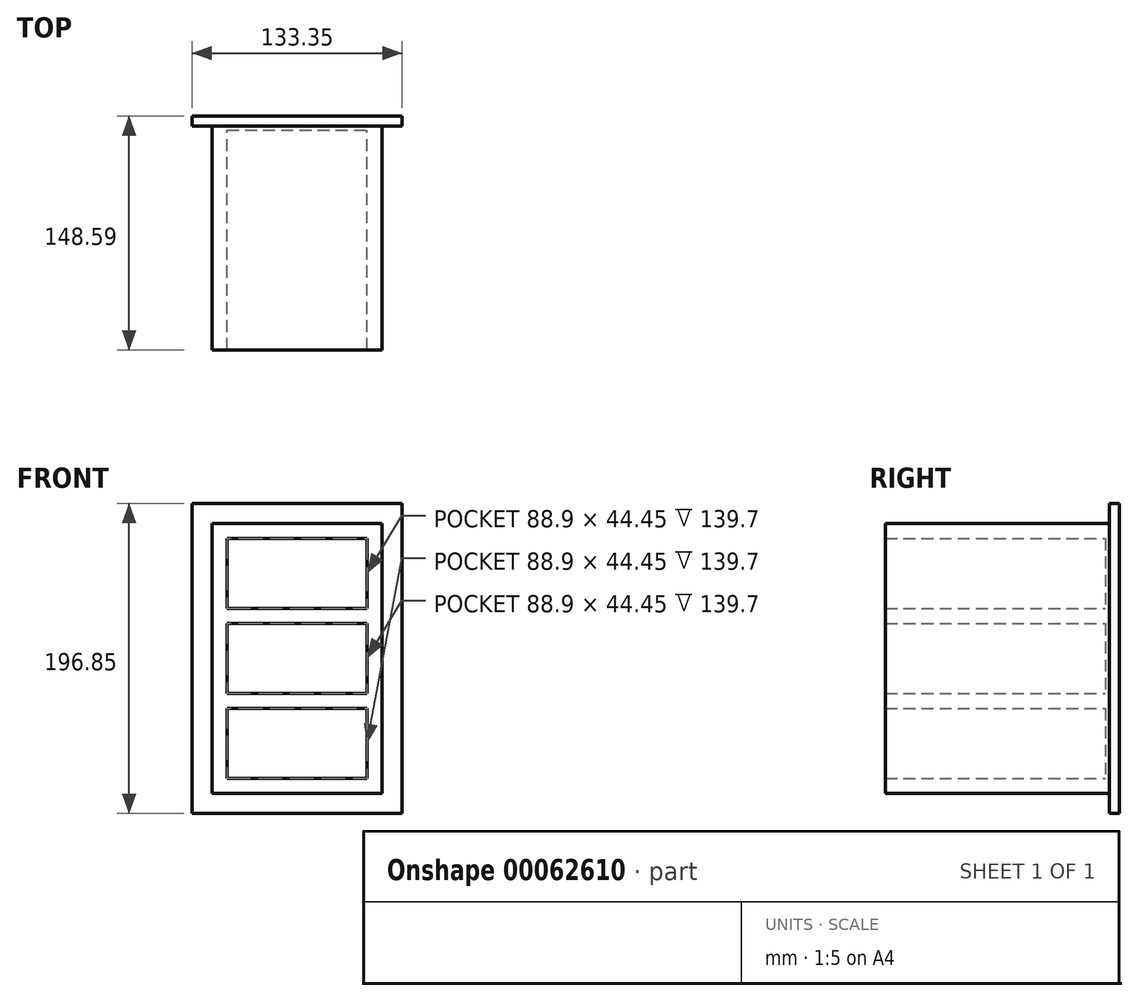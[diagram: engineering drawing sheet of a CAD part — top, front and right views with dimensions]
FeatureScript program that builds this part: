
annotation { "Feature Type Name" : "Feature", "Feature Type Description" : "" }
export const myFeature = defineFeature(function(context is Context, id is Id, definition is map)
    precondition{}
    {
        {
            var Q0;
            Q0=qCreatedBy(makeId("Front.planeOp"),FACE);
            var sketch = newSketch(context, id + "F0", { "sketchPlane" : qUnion([Q0])});
            skLineSegment(sketch, "E0.bottom", {"start": v(-98.78, 89.68) * mm, "end": v(-9.88, 89.68) * mm});
            skLineSegment(sketch, "E0.top", {"start": v(-98.78, -62.72) * mm, "end": v(-9.88, -62.72) * mm});
            skLineSegment(sketch, "E0.left", {"start": v(-98.78, 89.68) * mm, "end": v(-98.78, 45.23) * mm});
            skLineSegment(sketch, "E0.right", {"start": v(-9.88, 89.68) * mm, "end": v(-9.88, 45.23) * mm});
            skLineSegment(sketch, "E1.bottom", {"start": v(-98.78, 45.23) * mm, "end": v(-9.88, 45.23) * mm});
            skLineSegment(sketch, "E1.top", {"start": v(-98.78, 35.7) * mm, "end": v(-9.88, 35.7) * mm});
            skLineSegment(sketch, "E2", {"start": v(-98.78, 35.7) * mm, "end": v(-98.78, -8.75) * mm});
            skLineSegment(sketch, "E3.bottom", {"start": v(-98.78, -8.75) * mm, "end": v(-9.88, -8.75) * mm});
            skLineSegment(sketch, "E3.top", {"start": v(-98.78, -18.27) * mm, "end": v(-9.88, -18.27) * mm});
            skLineSegment(sketch, "E4", {"start": v(-98.78, -18.27) * mm, "end": v(-98.78, -62.72) * mm});
            skLineSegment(sketch, "E5.bottom", {"start": v(-108.3, 99.2) * mm, "end": v(-0.36, 99.2) * mm});
            skLineSegment(sketch, "E5.top", {"start": v(-108.3, -72.25) * mm, "end": v(-0.36, -72.25) * mm});
            skLineSegment(sketch, "E5.left", {"start": v(-108.3, 99.2) * mm, "end": v(-108.3, -72.25) * mm});
            skLineSegment(sketch, "E5.right", {"start": v(-0.36, 99.2) * mm, "end": v(-0.36, -72.25) * mm});
            skPoint(sketch, "E6.end.orphan", {"position": v(-108.3, 13.48) * mm});
            skPoint(sketch, "E6.start.orphan", {"position": v(-98.78, 13.48) * mm});
            skPoint(sketch, "E7.start.orphan", {"position": v(-54.33, 89.68) * mm});
            skPoint(sketch, "E8.end.orphan", {"position": v(-0.36, 13.48) * mm});
            skPoint(sketch, "E8.start.orphan", {"position": v(-9.88, 13.48) * mm});
            skPoint(sketch, "E9.start.orphan", {"position": v(-54.33, -62.72) * mm});
            skLineSegment(sketch, "E10.trimOffspring", {"start": v(-9.88, -18.27) * mm, "end": v(-9.88, -62.72) * mm});
            skLineSegment(sketch, "E11.trimOffspring", {"start": v(-9.88, 35.7) * mm, "end": v(-9.88, -8.75) * mm});
            skSolve(sketch);
        }
        {
            var Q0;
            Q0=makeQuery(id+"F0.imprint","IMPRINT",FACE,{"disambiguationData":[TD([[makeQuery(id+"F0.imprint","IMPRINT",EDGE,{"derivedFrom":sQuery(id+"F0.wireOp",EDGE,"E0.bottom")}),1.0]])]});
            extrude(context, id + "F1", {"entities" : qUnion([Q0]), "depth" : 139.7 * mm});
        }
        {
            var Q0;
            Q0=makeQuery(id+"F1.opExtrude","CAP_FACE",FACE,{"disambiguationData":[OSD([sQuery(id+"F0.wireOp",EDGE,"E0.bottom"),sQuery(id+"F0.wireOp",EDGE,"E0.top"),sQuery(id+"F0.wireOp",EDGE,"E0.right"),sQuery(id+"F0.wireOp",EDGE,"E0.left"),sQuery(id+"F0.wireOp",EDGE,"E1.bottom"),sQuery(id+"F0.wireOp",EDGE,"E1.top"),sQuery(id+"F0.wireOp",EDGE,"E3.bottom"),sQuery(id+"F0.wireOp",EDGE,"E3.top"),sQuery(id+"F0.wireOp",EDGE,"E5.bottom"),sQuery(id+"F0.wireOp",EDGE,"E5.top"),sQuery(id+"F0.wireOp",EDGE,"E5.left"),sQuery(id+"F0.wireOp",EDGE,"E5.right"),sQuery(id+"F0.wireOp",EDGE,"E2"),sQuery(id+"F0.wireOp",EDGE,"E4"),sQuery(id+"F0.wireOp",EDGE,"E10.trimOffspring"),sQuery(id+"F0.wireOp",EDGE,"E11.trimOffspring")])],"isStart":true});
            var sketch = newSketch(context, id + "F2", { "sketchPlane" : qUnion([Q0])});
            skLineSegment(sketch, "E12.bottom", {"start": v(0.36, 99.2) * mm, "end": v(108.3, 99.2) * mm});
            skLineSegment(sketch, "E12.top", {"start": v(0.36, -72.25) * mm, "end": v(108.3, -72.25) * mm});
            skLineSegment(sketch, "E12.left", {"start": v(0.36, 99.2) * mm, "end": v(0.36, -72.25) * mm});
            skLineSegment(sketch, "E12.right", {"start": v(108.3, 99.2) * mm, "end": v(108.3, -72.25) * mm});
            skSolve(sketch);
        }
        {
            var Q0;
            Q0 = qSketchRegion(id + "F2", true);
            extrude(context, id + "F3", {"entities" : qUnion([Q0]), "operationType" : NewBodyOperationType.ADD, "depth" : 2.54 * mm});
        }
        {
            var Q0;
            Q0=makeQuery(id+"F3.opExtrude","CAP_FACE",FACE,{"disambiguationData":[OSD([sQuery(id+"F2.wireOp",EDGE,"E12.bottom"),sQuery(id+"F2.wireOp",EDGE,"E12.top"),sQuery(id+"F2.wireOp",EDGE,"E12.left"),sQuery(id+"F2.wireOp",EDGE,"E12.right")])],"isStart":false});
            var sketch = newSketch(context, id + "F4", { "sketchPlane" : qUnion([Q0])});
            skLineSegment(sketch, "E13.top", {"start": v(0.36, 111.9) * mm, "end": v(-12.34, 111.9) * mm});
            skLineSegment(sketch, "E13.right", {"start": v(-12.34, 99.2) * mm, "end": v(-12.34, 111.9) * mm});
            skLineSegment(sketch, "E14.top", {"start": v(108.3, -84.95) * mm, "end": v(121, -84.95) * mm});
            skLineSegment(sketch, "E14.right", {"start": v(121, -72.25) * mm, "end": v(121, -84.95) * mm});
            skLineSegment(sketch, "E15.bottom", {"start": v(-12.34, 111.9) * mm, "end": v(121, 111.9) * mm});
            skLineSegment(sketch, "E15.top", {"start": v(-12.34, -84.95) * mm, "end": v(121, -84.95) * mm});
            skLineSegment(sketch, "E15.left", {"start": v(-12.34, 111.9) * mm, "end": v(-12.34, -84.95) * mm});
            skLineSegment(sketch, "E15.right", {"start": v(121, 111.9) * mm, "end": v(121, -84.95) * mm});
            skSolve(sketch);
        }
        {
            var Q0;
            Q0 = qSketchRegion(id + "F4", true);
            extrude(context, id + "F5", {"entities" : qUnion([Q0]), "operationType" : NewBodyOperationType.ADD, "depth" : 6.35 * mm});
        }
    });
